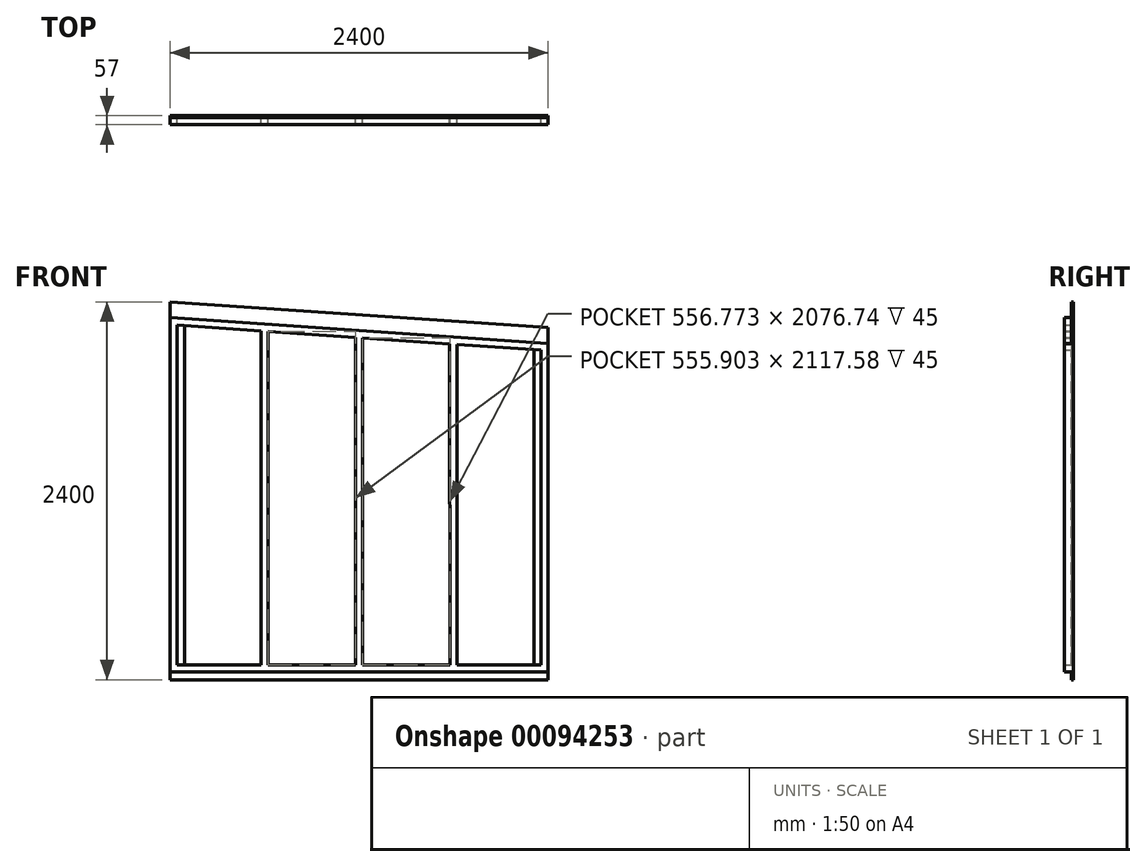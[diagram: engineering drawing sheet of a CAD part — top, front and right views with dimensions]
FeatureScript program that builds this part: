
annotation { "Feature Type Name" : "Feature", "Feature Type Description" : "" }
export const myFeature = defineFeature(function(context is Context, id is Id, definition is map)
    precondition{}
    {
        {
            var Q0;
            Q0=qCreatedBy(makeId("Front.planeOp"),FACE);
            var sketch = newSketch(context, id + "F0", { "sketchPlane" : qUnion([Q0])});
            skLineSegment(sketch, "E0.bottom", {"start": v(1200, -1175) * mm, "end": v(-1200, -1175) * mm});
            skLineSegment(sketch, "E0.left", {"start": v(1200, -1175) * mm, "end": v(1200, 1061.38) * mm});
            skLineSegment(sketch, "E0.right", {"start": v(-1200, -1175) * mm, "end": v(-1200, 1225) * mm});
            skLineSegment(sketch, "E1", {"start": v(-1200, 1225) * mm, "end": v(1200, 1061.38) * mm});
            skLineSegment(sketch, "E2", {"start": v(-1200, 1125.07) * mm, "end": v(1200, 961.45) * mm});
            skLineSegment(sketch, "E3", {"start": v(-1200, 1079.96) * mm, "end": v(1200, 916.35) * mm});
            skLineSegment(sketch, "E4", {"start": v(-1200, -1125) * mm, "end": v(1200, -1125) * mm});
            skLineSegment(sketch, "E5", {"start": v(1200, -1080) * mm, "end": v(-1200, -1080) * mm});
            skLineSegment(sketch, "E6", {"start": v(1155, -1080) * mm, "end": v(1155, 919.41) * mm});
            skLineSegment(sketch, "E7", {"start": v(-1155, 1076.9) * mm, "end": v(-1155, -1080) * mm});
            skLineSegment(sketch, "E8", {"start": v(-600, -1080) * mm, "end": v(-600, 1258.53) * mm, "construction": true});
            skLineSegment(sketch, "E9", {"start": v(0, 1332.7) * mm, "end": v(0, -1314.56) * mm, "construction": true});
            skLineSegment(sketch, "E10", {"start": v(600, 1227.21) * mm, "end": v(600, -1080) * mm, "construction": true});
            skLineSegment(sketch, "E11", {"start": v(-622.5, 1040.6) * mm, "end": v(-622.5, -1080) * mm});
            skLineSegment(sketch, "E12", {"start": v(-22.5, 999.69) * mm, "end": v(-22.5, -1080) * mm});
            skLineSegment(sketch, "E13.MirrorCS", {"start": v(622.5, 955.72) * mm, "end": v(622.5, -1080) * mm});
            skLineSegment(sketch, "E14.trimOffspring", {"start": v(-578.4, 1037.58) * mm, "end": v(-577.5, -1080) * mm});
            skPoint(sketch, "E15.MirrorCS.start.orphan", {"position": v(-577.5, 1258.61) * mm});
            skPoint(sketch, "E16.orphan", {"position": v(-622.5, 1258.61) * mm});
            skLineSegment(sketch, "E17.trimOffspring", {"start": v(20.73, 996.74) * mm, "end": v(22.5, -1080) * mm});
            skPoint(sketch, "E18.MirrorCS.start.orphan", {"position": v(22.5, 1253.07) * mm});
            skPoint(sketch, "E19.orphan", {"position": v(-22.5, 1253.07) * mm});
            skLineSegment(sketch, "E20.trimOffspring", {"start": v(574.92, 958.96) * mm, "end": v(577.5, -1080) * mm});
            skPoint(sketch, "E21.MirrorCS.start.orphan", {"position": v(577.5, 1258.61) * mm});
            skPoint(sketch, "E22.orphan", {"position": v(622.5, 1258.61) * mm});
            skLineSegment(sketch, "E23", {"start": v(-1110, 1073.83) * mm, "end": v(-1110, -1080) * mm});
            skLineSegment(sketch, "E24", {"start": v(-1065, 1070.76) * mm, "end": v(-1065, -1080) * mm});
            skLineSegment(sketch, "E25", {"start": v(1110, 922.48) * mm, "end": v(1110, -1080) * mm});
            skSolve(sketch);
        }
        {
            var Q0;
            {var subQ3=sQuery(id+"F0.wireOp",EDGE,"E2");Q0=makeQuery(id+"F0.imprint","IMPRINT",FACE,{"disambiguationData":[TD([[makeQuery(id+"F0.imprint","IMPRINT",EDGE,{"derivedFrom":subQ3}),-1.0]])]});}
            var Q1;
            {var subQ5=sQuery(id+"F0.wireOp",EDGE,"E7");Q1=makeQuery(id+"F0.imprint","IMPRINT",FACE,{"disambiguationData":[TD([[makeQuery(id+"F0.imprint","IMPRINT",EDGE,{"derivedFrom":subQ5}),-1.0]])]});}
            var Q2;
            {var subQ0=sQuery(id+"F0.wireOp",EDGE,"E11");Q2=makeQuery(id+"F0.imprint","IMPRINT",FACE,{"disambiguationData":[TD([[makeQuery(id+"F0.imprint","IMPRINT",EDGE,{"derivedFrom":subQ0}),1.0]])]});}
            var Q3;
            {var subQ0=sQuery(id+"F0.wireOp",EDGE,"E12");Q3=makeQuery(id+"F0.imprint","IMPRINT",FACE,{"disambiguationData":[TD([[makeQuery(id+"F0.imprint","IMPRINT",EDGE,{"derivedFrom":subQ0}),1.0]])]});}
            var Q4;
            {var subQ0=sQuery(id+"F0.wireOp",EDGE,"E13.MirrorCS");Q4=makeQuery(id+"F0.imprint","IMPRINT",FACE,{"disambiguationData":[TD([[makeQuery(id+"F0.imprint","IMPRINT",EDGE,{"derivedFrom":subQ0}),-1.0]])]});}
            var Q5;
            {var subQ5=sQuery(id+"F0.wireOp",EDGE,"E6");Q5=makeQuery(id+"F0.imprint","IMPRINT",FACE,{"disambiguationData":[TD([[makeQuery(id+"F0.imprint","IMPRINT",EDGE,{"derivedFrom":subQ5}),-1.0]])]});}
            var Q6;
            {var subQ12=sQuery(id+"F0.wireOp",EDGE,"E4");Q6=makeQuery(id+"F0.imprint","IMPRINT",FACE,{"disambiguationData":[TD([[makeQuery(id+"F0.imprint","IMPRINT",EDGE,{"derivedFrom":subQ12}),1.0]])]});}
            extrude(context, id + "F1", {"entities" : qUnion([Q0, Q1, Q2, Q3, Q4, Q5, Q6]), "depth" : 45 * mm});
        }
        {
            var Q0;
            {var subQ0=sQuery(id+"F0.wireOp",EDGE,"E7");Q0=makeQuery(id+"F0.imprint","IMPRINT",FACE,{"disambiguationData":[TD([[makeQuery(id+"F0.imprint","IMPRINT",EDGE,{"derivedFrom":subQ0}),1.0]])]});}
            var Q1;
            {var subQ0=sQuery(id+"F0.wireOp",EDGE,"E12");Q1=makeQuery(id+"F0.imprint","IMPRINT",FACE,{"disambiguationData":[TD([[makeQuery(id+"F0.imprint","IMPRINT",EDGE,{"derivedFrom":subQ0}),-1.0]])]});}
            var Q2;
            {var subQ0=sQuery(id+"F0.wireOp",EDGE,"E17.trimOffspring");Q2=makeQuery(id+"F0.imprint","IMPRINT",FACE,{"disambiguationData":[TD([[makeQuery(id+"F0.imprint","IMPRINT",EDGE,{"derivedFrom":subQ0}),1.0]])]});}
            var Q3;
            {var subQ0=sQuery(id+"F0.wireOp",EDGE,"E6");Q3=makeQuery(id+"F0.imprint","IMPRINT",FACE,{"disambiguationData":[TD([[makeQuery(id+"F0.imprint","IMPRINT",EDGE,{"derivedFrom":subQ0}),1.0]])]});}
            var Q4;
            {var subQ0=sQuery(id+"F0.wireOp",EDGE,"E1");Q4=makeQuery(id+"F0.imprint","IMPRINT",FACE,{"disambiguationData":[TD([[makeQuery(id+"F0.imprint","IMPRINT",EDGE,{"derivedFrom":subQ0}),-1.0]])]});}
            var Q5;
            {var subQ3=sQuery(id+"F0.wireOp",EDGE,"E2");Q5=makeQuery(id+"F0.imprint","IMPRINT",FACE,{"disambiguationData":[TD([[makeQuery(id+"F0.imprint","IMPRINT",EDGE,{"derivedFrom":subQ3}),-1.0]])]});}
            var Q6;
            {var subQ5=sQuery(id+"F0.wireOp",EDGE,"E7");Q6=makeQuery(id+"F0.imprint","IMPRINT",FACE,{"disambiguationData":[TD([[makeQuery(id+"F0.imprint","IMPRINT",EDGE,{"derivedFrom":subQ5}),-1.0]])]});}
            var Q7;
            {var subQ0=sQuery(id+"F0.wireOp",EDGE,"E11");Q7=makeQuery(id+"F0.imprint","IMPRINT",FACE,{"disambiguationData":[TD([[makeQuery(id+"F0.imprint","IMPRINT",EDGE,{"derivedFrom":subQ0}),1.0]])]});}
            var Q8;
            {var subQ0=sQuery(id+"F0.wireOp",EDGE,"E12");Q8=makeQuery(id+"F0.imprint","IMPRINT",FACE,{"disambiguationData":[TD([[makeQuery(id+"F0.imprint","IMPRINT",EDGE,{"derivedFrom":subQ0}),1.0]])]});}
            var Q9;
            {var subQ0=sQuery(id+"F0.wireOp",EDGE,"E13.MirrorCS");Q9=makeQuery(id+"F0.imprint","IMPRINT",FACE,{"disambiguationData":[TD([[makeQuery(id+"F0.imprint","IMPRINT",EDGE,{"derivedFrom":subQ0}),-1.0]])]});}
            var Q10;
            {var subQ5=sQuery(id+"F0.wireOp",EDGE,"E6");Q10=makeQuery(id+"F0.imprint","IMPRINT",FACE,{"disambiguationData":[TD([[makeQuery(id+"F0.imprint","IMPRINT",EDGE,{"derivedFrom":subQ5}),-1.0]])]});}
            var Q11;
            {var subQ12=sQuery(id+"F0.wireOp",EDGE,"E4");Q11=makeQuery(id+"F0.imprint","IMPRINT",FACE,{"disambiguationData":[TD([[makeQuery(id+"F0.imprint","IMPRINT",EDGE,{"derivedFrom":subQ12}),1.0]])]});}
            var Q12;
            {var subQ0=sQuery(id+"F0.wireOp",EDGE,"E0.bottom");Q12=makeQuery(id+"F0.imprint","IMPRINT",FACE,{"disambiguationData":[TD([[makeQuery(id+"F0.imprint","IMPRINT",EDGE,{"derivedFrom":subQ0}),-1.0]])]});}
            extrude(context, id + "F2", {"entities" : qUnion([Q0, Q1, Q2, Q3, Q4, Q5, Q6, Q7, Q8, Q9, Q10, Q11, Q12]), "operationType" : NewBodyOperationType.ADD, "oppositeDirection" : true, "depth" : 12 * mm});
        }
    });
